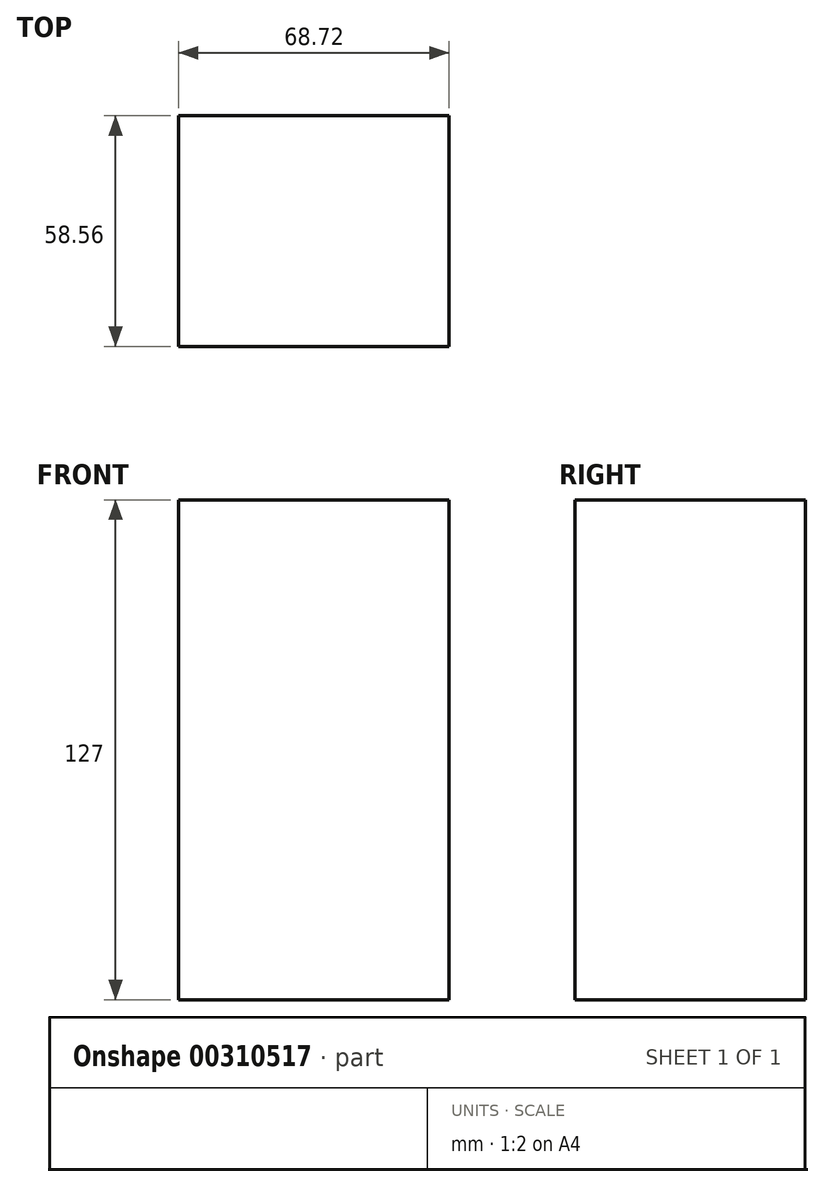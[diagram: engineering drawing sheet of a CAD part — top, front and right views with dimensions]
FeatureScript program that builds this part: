
annotation { "Feature Type Name" : "Feature", "Feature Type Description" : "" }
export const myFeature = defineFeature(function(context is Context, id is Id, definition is map)
    precondition{}
    {
        {
            var Q0;
            Q0=qCreatedBy(makeId("Top.planeOp"),FACE);
            var sketch = newSketch(context, id + "F0", { "sketchPlane" : qUnion([Q0])});
            skLineSegment(sketch, "E0.bottom", {"start": v(34.36, 29.28) * mm, "end": v(-34.36, 29.28) * mm});
            skLineSegment(sketch, "E0.top", {"start": v(34.36, -29.28) * mm, "end": v(-34.36, -29.28) * mm});
            skLineSegment(sketch, "E0.left", {"start": v(34.36, 29.28) * mm, "end": v(34.36, -29.28) * mm});
            skLineSegment(sketch, "E0.right", {"start": v(-34.36, 29.28) * mm, "end": v(-34.36, -29.28) * mm});
            skPoint(sketch, "E0.middle", {"position": v(0, 0) * mm});
            skSolve(sketch);
        }
        {
            var Q0;
            Q0 = qSketchRegion(id + "F0", true);
            extrude(context, id + "F1", {"entities" : qUnion([Q0]), "depth" : 127 * mm});
        }
    });
